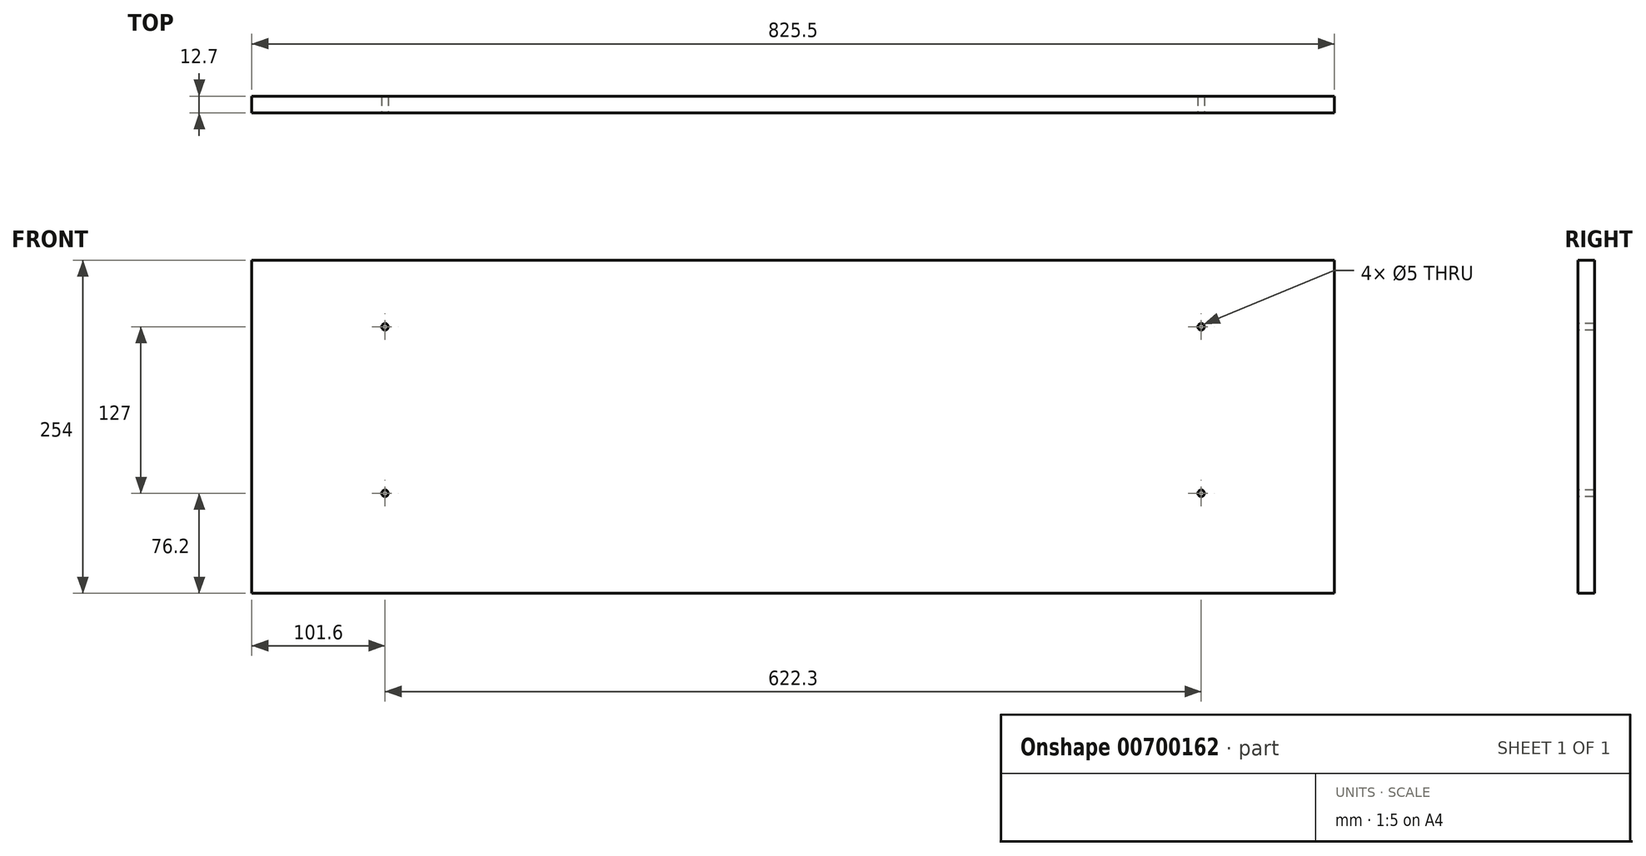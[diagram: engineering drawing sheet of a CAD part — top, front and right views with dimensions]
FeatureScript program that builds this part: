
annotation { "Feature Type Name" : "Feature", "Feature Type Description" : "" }
export const myFeature = defineFeature(function(context is Context, id is Id, definition is map)
    precondition{}
    {
        {
            var Q0;
            Q0=qCreatedBy(makeId("Front.planeOp"),FACE);
            var sketch = newSketch(context, id + "F0", { "sketchPlane" : qUnion([Q0])});
            skLineSegment(sketch, "E0.bottom", {"start": v(412.75, -127) * mm, "end": v(-412.75, -127) * mm});
            skLineSegment(sketch, "E0.top", {"start": v(412.75, 127) * mm, "end": v(-412.75, 127) * mm});
            skLineSegment(sketch, "E0.left", {"start": v(412.75, -127) * mm, "end": v(412.75, 127) * mm});
            skLineSegment(sketch, "E0.right", {"start": v(-412.75, -127) * mm, "end": v(-412.75, 127) * mm});
            skPoint(sketch, "E0.middle", {"position": v(0, 0) * mm});
            skSolve(sketch);
        }
        {
            var Q0;
            Q0=makeQuery(id+"F0.imprint","IMPRINT",FACE,{"disambiguationData":[TD([[makeQuery(id+"F0.imprint","IMPRINT",EDGE,{"derivedFrom":sQuery(id+"F0.wireOp",EDGE,"E0.bottom")}),-1.0]])]});
            extrude(context, id + "F1", {"entities" : qUnion([Q0]), "depth" : 12.7 * mm, "offsetDistance" : 25.4 * mm});
        }
        {
            var Q0;
            Q0=makeQuery(id+"F1.opExtrude","CAP_FACE",FACE,{"disambiguationData":[OSD([sQuery(id+"F0.wireOp",EDGE,"E0.bottom"),sQuery(id+"F0.wireOp",EDGE,"E0.top"),sQuery(id+"F0.wireOp",EDGE,"E0.left"),sQuery(id+"F0.wireOp",EDGE,"E0.right")])],"isStart":false});
            var sketch = newSketch(context, id + "F2", { "sketchPlane" : qUnion([Q0])});
            skLineSegment(sketch, "E1", {"start": v(-412.75, 127) * mm, "end": v(-311.15, 127) * mm});
            skLineSegment(sketch, "E2", {"start": v(-311.15, 127) * mm, "end": v(-311.15, 76.2) * mm});
            skLineSegment(sketch, "E3", {"start": v(-412.75, -127) * mm, "end": v(-311.15, -127) * mm});
            skLineSegment(sketch, "E4", {"start": v(-311.15, -127) * mm, "end": v(-311.15, -50.8) * mm});
            skLineSegment(sketch, "E5", {"start": v(412.75, 127) * mm, "end": v(311.15, 127) * mm});
            skLineSegment(sketch, "E6", {"start": v(311.15, 127) * mm, "end": v(311.15, 76.2) * mm});
            skLineSegment(sketch, "E7", {"start": v(412.75, -127) * mm, "end": v(311.15, -127) * mm});
            skLineSegment(sketch, "E8", {"start": v(311.15, -127) * mm, "end": v(311.15, -50.8) * mm});
            skPoint(sketch, "E9", {"position": v(-311.15, 76.2) * mm});
            skPoint(sketch, "E10", {"position": v(-311.15, -50.8) * mm});
            skPoint(sketch, "E11", {"position": v(311.15, -50.8) * mm});
            skPoint(sketch, "E12", {"position": v(311.15, 76.2) * mm});
            skSolve(sketch);
        }
        {
            var Q0;
            Q0=sQuery(id+"F2.wireOp",VERTEX,"E9");
            var Q1;
            Q1=sQuery(id+"F2.wireOp",VERTEX,"E10");
            var Q2;
            Q2=sQuery(id+"F2.wireOp",VERTEX,"E12");
            var Q3;
            Q3=sQuery(id+"F2.wireOp",VERTEX,"E11");
            var Q4;
            Q4=makeQuery(id+"F1.opExtrude","SWEPT_BODY",BODY,{"disambiguationData":[OSD([sQuery(id+"F0.wireOp",EDGE,"E0.bottom"),sQuery(id+"F0.wireOp",EDGE,"E0.top"),sQuery(id+"F0.wireOp",EDGE,"E0.left"),sQuery(id+"F0.wireOp",EDGE,"E0.right")])]});
            hole(context, id + "F3", {"style" : HoleStyle.SIMPLE, "endStyle" : HoleEndStyle.BLIND, "holeDiameter" : 5 * mm, "majorDiameter" : 6.35 * mm, "holeDepth" : 14.22 * mm, "isTappedThrough" : true, "tappedDepth" : 12.7 * mm, "tapClearance" : 3, "startFromSketch" : true, "locations" : qUnion([Q0, Q1, Q2, Q3]), "scope" : qUnion([Q4])});
        }
    });
